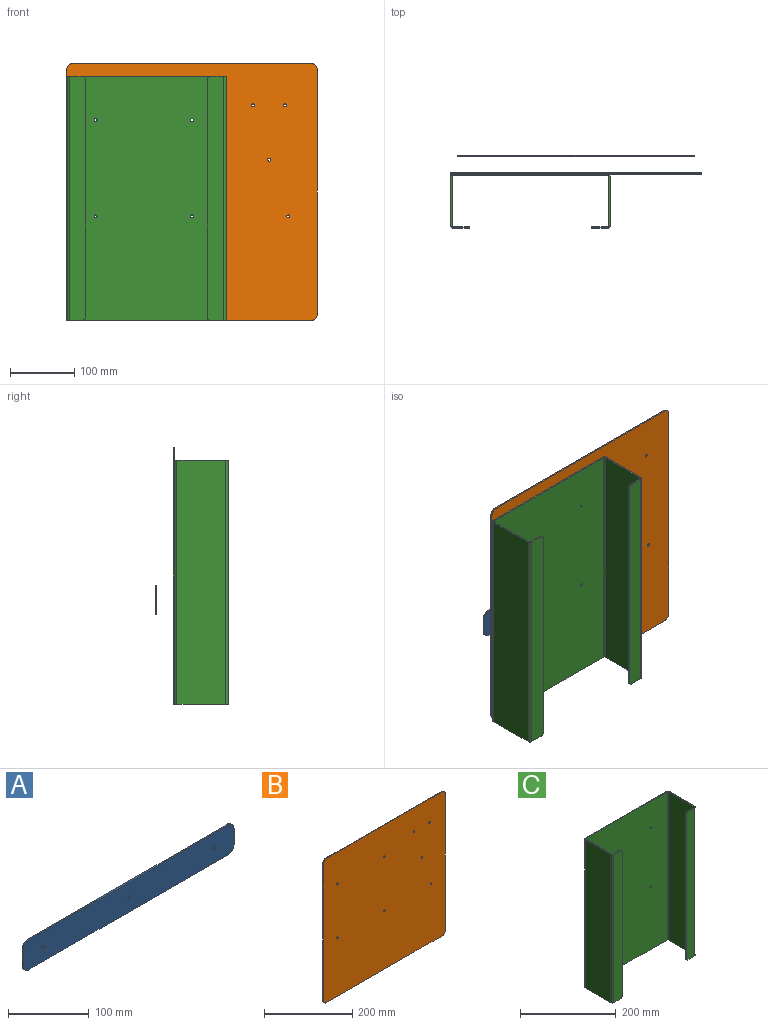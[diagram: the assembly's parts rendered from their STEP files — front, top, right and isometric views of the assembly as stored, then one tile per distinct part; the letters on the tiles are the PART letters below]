
ASSEMBLY  parts=3 mates=2
PART A: 13 faces, bbox 370x2x45 mm
  f0: plane 350x2mm, normal (0,0,1), area 700mm2, adj f4,f5,f9,f12
  f1: plane 25x2mm, normal (-1,0,0), area 50mm2, adj f4,f5,f9,f10
  f2: plane 350x2mm, normal (0,0,-1), area 700mm2, adj f4,f5,f10,f11
  f3: plane 25x2mm, normal (1,0,0), area 50mm2, adj f4,f5,f11,f12
  f4: plane 370x45mm, normal (0,-1,0), area 16516.4mm2, adj f0,f1,f2,f3,f6,f7,f8,f9
  f5: plane 370x45mm, normal (0,1,0), area 16516.4mm2, adj f0,f1,f2,f3,f6,f7,f8,f9
  f6: cylinder r=2.25mm len=4.5mm, axis (0,-1,0), area 28.3mm2, adj f4,f5
  f7: cylinder r=2.25mm len=4.5mm, axis (0,-1,0), area 28.3mm2, adj f4,f5
  f8: cylinder r=2.25mm len=4.5mm, axis (0,-1,0), area 28.3mm2, adj f4,f5
  f9: cylinder r=10mm len=10mm, axis (0,1,0), area 31.4mm2, adj f0,f1,f4,f5
  f10: cylinder r=10mm len=10mm, axis (0,-1,0), area 31.4mm2, adj f1,f2,f4,f5
  f11: cylinder r=10mm len=10mm, axis (0,1,0), area 31.4mm2, adj f2,f3,f4,f5
  f12: cylinder r=10mm len=10mm, axis (0,-1,0), area 31.4mm2, adj f0,f3,f4,f5
PART B: 18 faces, bbox 390x2x400 mm
  f0: plane 370x2mm, normal (0,0,1), area 740mm2, adj f4,f5,f14,f17
  f1: plane 380x2mm, normal (-1,0,0), area 760mm2, adj f4,f5,f14,f15
  f2: plane 370x2mm, normal (0,0,-1), area 740mm2, adj f4,f5,f15,f16
  f3: plane 380x2mm, normal (1,0,0), area 760mm2, adj f4,f5,f16,f17
  f4: plane 400x390mm, normal (0,-1,0), area 155786.9mm2, adj f0,f1,f2,f3,f6,f7,f8,f9
  f5: plane 400x390mm, normal (0,1,0), area 155786.9mm2, adj f0,f1,f2,f3,f6,f7,f8,f9
  f6: cylinder r=2.25mm len=4.5mm, axis (0,-1,0), area 28.3mm2, adj f4,f5
  f7: cylinder r=2.25mm len=4.5mm, axis (0,-1,0), area 28.3mm2, adj f4,f5
  f8: cylinder r=2.25mm len=4.5mm, axis (0,-1,0), area 28.3mm2, adj f4,f5
  f9: cylinder r=2.25mm len=4.5mm, axis (0,-1,0), area 28.3mm2, adj f4,f5
  f10: cylinder r=2.25mm len=4.5mm, axis (0,-1,0), area 28.3mm2, adj f4,f5
  f11: cylinder r=2.25mm len=4.5mm, axis (0,-1,0), area 28.3mm2, adj f4,f5
  f12: cylinder r=2.25mm len=4.5mm, axis (0,-1,0), area 28.3mm2, adj f4,f5
  f13: cylinder r=2.25mm len=4.5mm, axis (0,-1,0), area 28.3mm2, adj f4,f5
  f14: cylinder r=10mm len=10mm, axis (0,1,0), area 31.4mm2, adj f0,f1,f4,f5
  f15: cylinder r=10mm len=10mm, axis (0,-1,0), area 31.4mm2, adj f1,f2,f4,f5
  f16: cylinder r=10mm len=10mm, axis (0,1,0), area 31.4mm2, adj f2,f3,f4,f5
  f17: cylinder r=10mm len=10mm, axis (0,-1,0), area 31.4mm2, adj f0,f3,f4,f5
PART C: 30 faces, bbox 248x84x380 mm
  f0: plane 380x25mm, normal (0,1,0), area 9489.3mm2, adj f11,f12,f13,f14,f27,f29
  f1: plane 380x76mm, normal (1,0,0), area 28880mm2, adj f12,f13,f14,f15
  f2: plane 380x240mm, normal (0,-1,0), area 91136.4mm2, adj f12,f13,f15,f16,f22,f23,f24,f25
  f3: plane 380x76mm, normal (-1,0,0), area 28880mm2, adj f12,f13,f16,f17
  f4: plane 380x25mm, normal (0,1,0), area 9489.3mm2, adj f5,f12,f13,f17,f26,f28
  f5: plane 370x2mm, normal (-1,0,0), area 740mm2, adj f4,f6,f26,f28
  f6: plane 380x25mm, normal (0,-1,0), area 9489.3mm2, adj f5,f12,f13,f18,f26,f28
  f7: plane 380x76mm, normal (1,0,0), area 28880mm2, adj f12,f13,f18,f19
  f8: plane 380x240mm, normal (0,1,0), area 91136.4mm2, adj f12,f13,f19,f20,f22,f23,f24,f25
  f9: plane 380x76mm, normal (-1,0,0), area 28880mm2, adj f12,f13,f20,f21
  f10: plane 380x25mm, normal (0,-1,0), area 9489.3mm2, adj f11,f12,f13,f21,f27,f29
  f11: plane 370x2mm, normal (1,0,0), area 740mm2, adj f0,f10,f27,f29
  f12: plane 248x84mm, normal (0,0,1), area 901.7mm2, adj f0,f1,f2,f3,f4,f6,f7,f8
  f13: plane 248x84mm, normal (0,0,-1), area 901.7mm2, adj f0,f1,f2,f3,f4,f6,f7,f8
  f14: cylinder r=2mm len=380mm, axis (0,0,1), area 1193.8mm2, adj f0,f1,f12,f13
  f15: cylinder r=2mm len=380mm, axis (0,0,1), area 1193.8mm2, adj f1,f2,f12,f13
  f16: cylinder r=2mm len=380mm, axis (0,0,1), area 1193.8mm2, adj f2,f3,f12,f13
  f17: cylinder r=2mm len=380mm, axis (0,0,1), area 1193.8mm2, adj f3,f4,f12,f13
  f18: cylinder r=4mm len=380mm, axis (0,0,-1), area 2387.6mm2, adj f6,f7,f12,f13
  f19: cylinder r=4mm len=380mm, axis (0,0,-1), area 2387.6mm2, adj f7,f8,f12,f13
  f20: cylinder r=4mm len=380mm, axis (0,0,-1), area 2387.6mm2, adj f8,f9,f12,f13
  f21: cylinder r=4mm len=380mm, axis (0,0,-1), area 2387.6mm2, adj f9,f10,f12,f13
  f22: cylinder r=2.25mm len=4.5mm, axis (0,1,0), area 28.3mm2, adj f2,f8
  f23: cylinder r=2.25mm len=4.5mm, axis (0,1,0), area 28.3mm2, adj f2,f8
  f24: cylinder r=2.25mm len=4.5mm, axis (0,1,0), area 28.3mm2, adj f2,f8
  f25: cylinder r=2.25mm len=4.5mm, axis (0,1,0), area 28.3mm2, adj f2,f8
  f26: cylinder r=5mm len=5mm, axis (0,-1,0), area 15.7mm2, adj f4,f5,f6,f13
  f27: cylinder r=5mm len=5mm, axis (0,1,0), area 15.7mm2, adj f0,f10,f11,f13
  f28: cylinder r=5mm len=5mm, axis (0,1,0), area 15.7mm2, adj f4,f5,f6,f12
  f29: cylinder r=5mm len=5mm, axis (0,-1,0), area 15.7mm2, adj f0,f10,f11,f12
PLACE A t=(38.64,207.86,281.72)mm
PLACE B t=(38.64,180.86,142.22)mm fixed
PLACE C t=(-156.36,178.86,142.22)mm
MATE fastened A.f6 <-> B.f11  axis (0,-1,0) through (38.64,205.86,304.22)mm
MATE fastened C.f9 <-> B.f1  axis (-1,0,0) through (-156.36,136.86,332.22)mm
